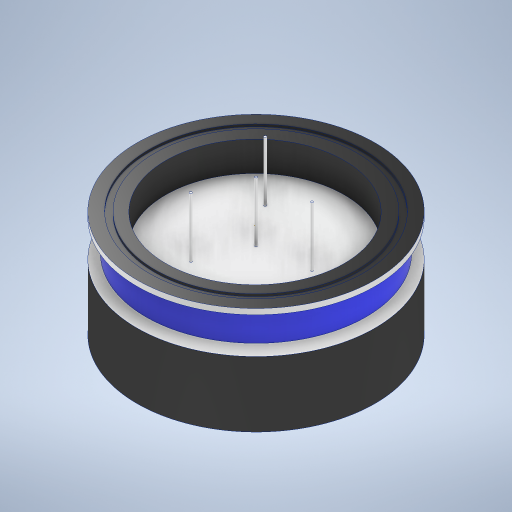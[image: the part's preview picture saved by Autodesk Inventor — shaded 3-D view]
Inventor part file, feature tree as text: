
AUTODESK INVENTOR PART (.ipt)
format: ipt  version: 2024 (Build 280153000, 153)  size: 339,456 bytes
history: native  units: mm
features: extrude x5, sketch x4, revolve x1
ambient origin geometry x8: Origin, YZ Plane, XZ Plane, XY Plane, X Axis, Y Axis, Z Axis, Center Point
bodies: Solid1 (feature_tree)
feature tree (10):
  sketch  "Sketch1"  dims[d0=200.0mm d1=180.0mm]
  extrude  "Extrusion1"  Depth=180.0mm
  extrude  "Extrusion2"  Depth=8.0mm TaperAngle=0.0deg
  extrude  "Extrusion3"  Depth=80.0mm TaperAngle=0.0deg
  extrude  "Extrusion4"  Depth=25.0mm TaperAngle=0.0deg
  revolve  "Revolution1"  Angle=120.0deg
  extrude  "Extrusion7"  TaperAngle=60.0deg  [1 undecoded]
  sketch  "Sketch2"  dims[d2=170.0mm d3=8.0mm d4=0.0mm]
  sketch  "Sketch3"  dims[d5=10.0mm d6=0.0mm d7=80.0mm d8=0.0mm]
  sketch  "Sketch6"  dims[d9=150.0mm d10=25.0mm d11=0.0mm d12=120.0deg d13=60.0deg d14=90.0deg d32=84.0mm d33=2.0mm d34=30.0mm d36=360.0deg d38=50.0mm d39=0.0mm d40=2.0mm]
note: 1 required parameter value undecoded (feature->parameter linkage not recoverable at this tier; creation-order binding heuristic only, values carry confidence <= 0.55)
